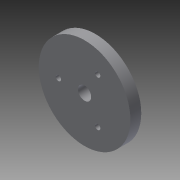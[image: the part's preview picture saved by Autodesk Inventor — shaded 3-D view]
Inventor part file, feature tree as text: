
AUTODESK INVENTOR PART (.ipt)
format: ipt  version: 2015 (Build 190159000, 159)  size: 129,024 bytes
history: native  units: mm
features: sketch x7, extrude x6
ambient origin geometry x8: Origin, YZ Plane, XZ Plane, XY Plane, X Axis, Y Axis, Z Axis, Center Point
bodies: Solid1 (feature_tree)
feature tree (13):
  extrude  "Extrusion1"  Depth=5.0mm
  extrude  "Extrusion2"  Depth=3.0mm
  extrude  "Extrusion3"  Depth=3.0mm
  extrude  "Extrusion4"  Depth=34.65mm
  extrude  "Extrusion5"  Depth=3.8mm TaperAngle=0.0deg
  sketch  "Sketch6"  dims[d16=2.0mm d19=2.0mm]
  extrude  "Extrusion6"  Depth=2.0mm
  sketch  "Sketch1"  dims[d0=33.15mm d1=5.0mm]
  sketch  "Sketch2"  dims[d2=3.8mm d3=0.0mm d4=3.0mm]
  sketch  "Sketch3"  dims[d7=3.0mm d8=3.0mm]
  sketch  "Sketch4"  dims[d9=3.8mm d10=0.0mm d11=34.65mm]
  sketch  "Sketch5"  dims[d12=3.8mm d13=0.0mm d14=3.8mm d15=0.0mm]
  sketch  "Sketch7"  dims[d20=2.0mm d21=3.8mm d22=0.0mm d23=0.3mm d24=0.0mm]
